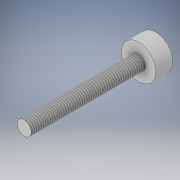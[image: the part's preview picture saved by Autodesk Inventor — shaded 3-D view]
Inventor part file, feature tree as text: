
AUTODESK INVENTOR PART (.ipt)
format: ipt  version: 2018 (Build 220112000, 112)  size: 107,520 bytes
history: native  units: in
note: dims shown in document units (in); Inventor stores cm internally (conversion verified against a paired STEP export)
features: revolve x1, thread x1, sketch x1
ambient origin geometry x8: Origin, YZ Plane, XZ Plane, XY Plane, X Axis, Y Axis, Z Axis, Center Point
bodies: Solid1 (feature_tree)
feature tree (3):
  revolve  "Revolution1"  [1 undecoded]
  thread  "Thread1"  [1 undecoded]
  sketch  "Sketch1"  dims[d0=0.0984in d1=1.5748in d2=0.2362in d3=0.2362in d4=90.0deg d5=0.3937in d6=0.0in]
note: 2 required parameter values undecoded (feature->parameter linkage not recoverable at this tier; creation-order binding heuristic only, values carry confidence <= 0.55)